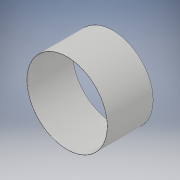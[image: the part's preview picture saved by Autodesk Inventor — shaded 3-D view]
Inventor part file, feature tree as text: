
AUTODESK INVENTOR PART (.ipt)
format: ipt  version: 2019 (Build 230136000, 136)  size: 103,424 bytes
history: native  units: mm
features: extrude x2, sketch x2
ambient origin geometry x8: Origin, YZ Plane, XZ Plane, XY Plane, X Axis, Y Axis, Z Axis, Center Point
bodies: Solid1 (feature_tree)
feature tree (4):
  extrude  "Extrusion1"  Depth=11.51mm TaperAngle=0.0deg
  extrude  "Extrusion2"  Depth=11.51mm TaperAngle=0.0deg
  sketch  "Sketch1"  dims[d0=20.27mm d1=11.51mm d2=0.0mm]
  sketch  "Sketch2"  dims[d3=20.17mm d4=11.51mm d5=0.0mm]
